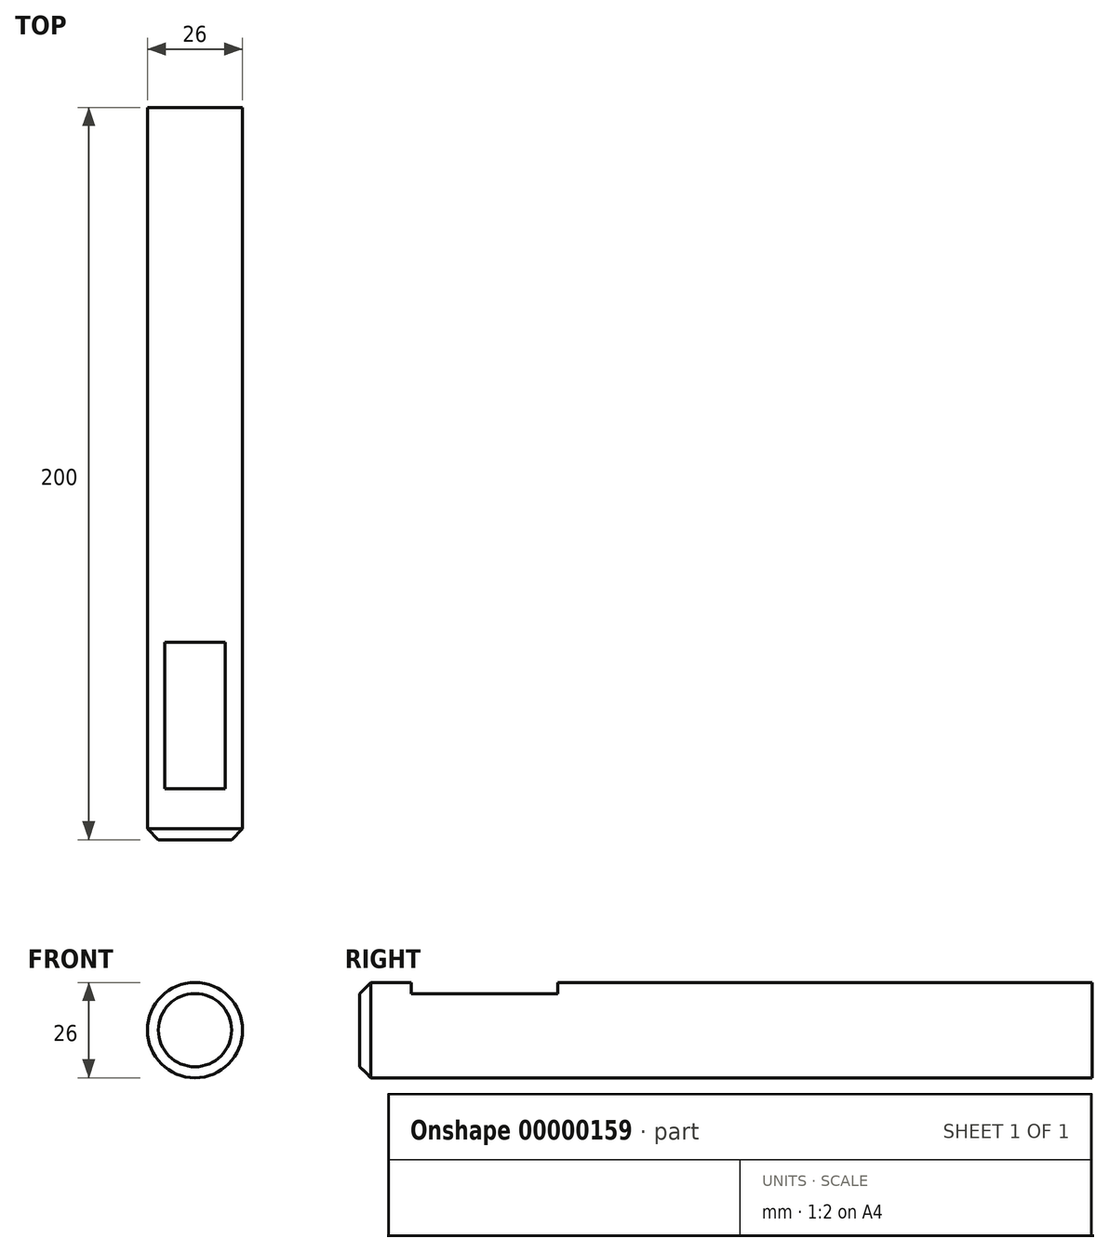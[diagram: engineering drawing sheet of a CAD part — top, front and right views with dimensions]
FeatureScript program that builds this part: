
annotation { "Feature Type Name" : "Feature", "Feature Type Description" : "" }
export const myFeature = defineFeature(function(context is Context, id is Id, definition is map)
    precondition{}
    {
        {
            var Q0;
            Q0=qCreatedBy(makeId("Front.planeOp"),FACE);
            var sketch = newSketch(context, id + "F0", { "sketchPlane" : qUnion([Q0])});
            skCircle(sketch, "E0", {"center": v(0, 0) * mm, "radius": 13 * mm});
            skSolve(sketch);
        }
        {
            var Q0;
            Q0=makeQuery(id+"F0.imprint","IMPRINT",FACE,{"disambiguationData":[TD([[makeQuery(id+"F0.imprint","IMPRINT",EDGE,{"derivedFrom":sQuery(id+"F0.wireOp",EDGE,"E0")}),1.0]])]});
            extrude(context, id + "F1", {"entities" : qUnion([Q0]), "depth" : 200 * mm});
        }
        {
            var Q0;
            Q0=makeQuery(id+"F1.opExtrude","CAP_EDGE",EDGE,{"disambiguationData":[OSD([sQuery(id+"F0.wireOp",EDGE,"E0")])],"isStart":false});
            chamfer(context, id + "F2", {"entities" : qUnion([Q0]), "width" : 3 * mm, "tangentPropagation" : true});
        }
        {
            var Q0;
            Q0=qCreatedBy(makeId("Top.planeOp"),FACE);
            cPlane(context, id + "F3", {"entities" : qUnion([Q0]), "cplaneType" : CPlaneType.OFFSET, "offset" : 10 * mm, "width" : 400 * mm, "height" : 400 * mm});
        }
        {
            var Q0;
            Q0=qCreatedBy(id+"F3.planeOp",FACE);
            var sketch = newSketch(context, id + "F4", { "sketchPlane" : qUnion([Q0])});
            skLineSegment(sketch, "E1", {"start": v(32, -186) * mm, "end": v(32, -146) * mm});
            skLineSegment(sketch, "E2", {"start": v(0, 0) * mm, "end": v(0, -242.5) * mm, "construction": true});
            skLineSegment(sketch, "E3.0.MirrorCS", {"start": v(-32, -186) * mm, "end": v(-32, -146) * mm});
            skLineSegment(sketch, "E4", {"start": v(32, -146) * mm, "end": v(-32, -146) * mm});
            skLineSegment(sketch, "E5", {"start": v(-32, -186) * mm, "end": v(32, -186) * mm});
            skSolve(sketch);
        }
        {
            var Q0;
            Q0=makeQuery(id+"F4.imprint","IMPRINT",FACE,{"disambiguationData":[TD([[makeQuery(id+"F4.imprint","IMPRINT",EDGE,{"derivedFrom":sQuery(id+"F4.wireOp",EDGE,"E1")}),1.0]])]});
            extrude(context, id + "F5", {"entities" : qUnion([Q0]), "operationType" : NewBodyOperationType.REMOVE, "depth" : 25 * mm});
        }
    });
